# Revit family: Toilet-Elongated-Right_Height-American_Standard-Edgemere-204AA10X
name_source: partatom
category: Plumbing Fixtures
revit_build: Autodesk Revit 2014 (Build: 20130308_1515(x64)
units: mm (PartAtom-declared; Revit-internal decimal feet)

## types (2) — shared parameters
ADA Compliant = Yes
Assembly Code = D2010110
Bowl Shape = Elongated
CW Connection = Yes
CWFU = 3
Cold Water Connection Diameter = 1/2"
Cold Water Connection Height = 8"
Cold Water Connection Radius = 1/4"
Cold Water Connection Width = 6"
Default Elevation = 0"
EPA WaterSense = Yes
EverClean Surface = Yes
Finish = Vitreous China-American Standard-020-White
Flush Rate = 1.28Gpf (4.8Lpf)
HW Connection = No
Height = 31 1/8"
Installation Type = Floor Mounted
Length = 30 3/16"
Manufacturer = American Standard
Material = Vitreous China-American Standard-020-White
Price = Prices may vary. Please consult Manufacturer Representative for most up-to-date price list.
Product Documentation Link = https://www.americanstandard-us.com
Product URL = https://www.americanstandard-us.com
URL = http://www.americanstandard-us.com
Vent Connection = No
WFU = 3
Warranty Information = 5 Year Limited
Waste Connection = Yes
Waste Connection Diameter = 2"
Waste Connection Radius = 1"
Width = 17"
zero-valued in all types: HWFU

## per-type parameters (varying)
| type | Description | Left Trip Lever | Right Trip Lever |
| 204AA104 | 204AA104 Edgemere Right Height Elongated 12" Rough Toilet trip lever on left hand side | Yes | No |
| 204AA105 | 204AA105 Edgemere Right Height Elongated 12" Rough Toilet trip lever on Right hand side | No | Yes |

note: column(s) folded — value = type name in every type: Model

## geometry (parser evidence)
native form markers: Sweep x1
no freeform markers — native parametric forms only
